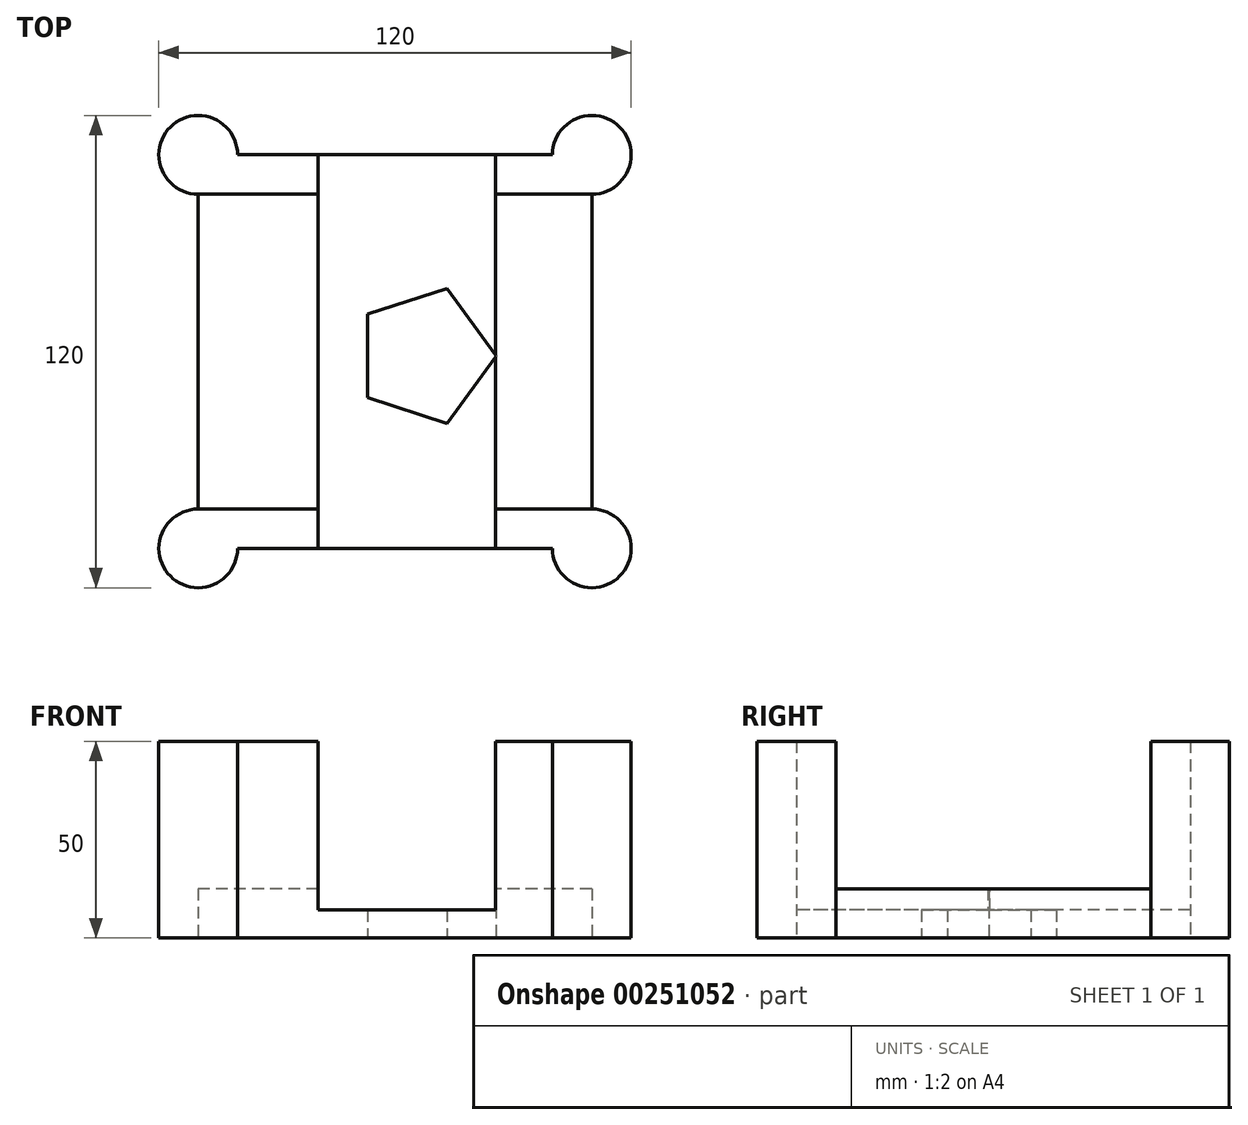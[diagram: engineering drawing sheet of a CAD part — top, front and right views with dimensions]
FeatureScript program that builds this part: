
annotation { "Feature Type Name" : "Feature", "Feature Type Description" : "" }
export const myFeature = defineFeature(function(context is Context, id is Id, definition is map)
    precondition{}
    {
        {
            var Q0;
            Q0=qCreatedBy(makeId("Top.planeOp"),FACE);
            var sketch = newSketch(context, id + "F0", { "sketchPlane" : qUnion([Q0])});
            skLineSegment(sketch, "E0.bottom", {"start": v(-57.64, -48.48) * mm, "end": v(42.36, -48.48) * mm});
            skLineSegment(sketch, "E0.top", {"start": v(-57.64, 51.52) * mm, "end": v(42.36, 51.52) * mm});
            skLineSegment(sketch, "E0.left", {"start": v(-57.64, -48.48) * mm, "end": v(-57.64, 51.52) * mm});
            skLineSegment(sketch, "E0.right", {"start": v(42.36, -48.48) * mm, "end": v(42.36, 51.52) * mm});
            skSolve(sketch);
        }
        {
            var Q0;
            Q0 = qSketchRegion(id + "F0", true);
            extrude(context, id + "F1", {"entities" : qUnion([Q0]), "depth" : 50 * mm});
        }
        {
            var Q0;
            Q0=makeQuery(id+"F1.opExtrude","SWEPT_FACE",FACE,{"disambiguationData":[OSD([sQuery(id+"F0.wireOp",EDGE,"E0.bottom")])]});
            var sketch = newSketch(context, id + "F2", { "sketchPlane" : qUnion([Q0])});
            skLineSegment(sketch, "E1.bottom", {"start": v(-27.14, 52.1) * mm, "end": v(17.86, 52.1) * mm});
            skLineSegment(sketch, "E1.top", {"start": v(-27.14, 7.1) * mm, "end": v(17.86, 7.1) * mm});
            skLineSegment(sketch, "E1.left", {"start": v(-27.14, 52.1) * mm, "end": v(-27.14, 7.1) * mm});
            skLineSegment(sketch, "E1.right", {"start": v(17.86, 52.1) * mm, "end": v(17.86, 7.1) * mm});
            skPoint(sketch, "E2.firstSnap0", {"position": v(-4.64, 52.1) * mm});
            skLineSegment(sketch, "E2.bottom", {"start": v(0, 52.1) * mm, "end": v(0, 52.1) * mm});
            skLineSegment(sketch, "E2.top", {"start": v(0, 33.97) * mm, "end": v(0, 33.97) * mm});
            skLineSegment(sketch, "E2.left", {"start": v(0, 52.1) * mm, "end": v(0, 33.97) * mm});
            skLineSegment(sketch, "E2.right", {"start": v(0, 52.1) * mm, "end": v(0, 33.97) * mm});
            skSolve(sketch);
        }
        {
            var Q0;
            Q0 = qSketchRegion(id + "F2", true);
            extrude(context, id + "F3", {"entities" : qUnion([Q0]), "operationType" : NewBodyOperationType.REMOVE, "oppositeDirection" : true, "depth" : 100 * mm});
        }
        {
            var Q0;
            Q0=makeQuery(id+"F1.opExtrude","CAP_FACE",FACE,{"disambiguationData":[OSD([sQuery(id+"F0.wireOp",EDGE,"E0.bottom"),sQuery(id+"F0.wireOp",EDGE,"E0.top"),sQuery(id+"F0.wireOp",EDGE,"E0.left"),sQuery(id+"F0.wireOp",EDGE,"E0.right")])],"isStart":true});
            var sketch = newSketch(context, id + "F4", { "sketchPlane" : qUnion([Q0])});
            skCircle(sketch, "E3", {"center": v(-57.64, -51.52) * mm, "radius": 10 * mm});
            skCircle(sketch, "E4", {"center": v(-57.64, 48.48) * mm, "radius": 10 * mm});
            skCircle(sketch, "E5", {"center": v(42.36, 48.48) * mm, "radius": 10 * mm});
            skCircle(sketch, "E6", {"center": v(42.36, -51.52) * mm, "radius": 10 * mm});
            skSolve(sketch);
        }
        {
            var Q0;
            Q0 = qSketchRegion(id + "F4", true);
            extrude(context, id + "F5", {"entities" : qUnion([Q0]), "operationType" : NewBodyOperationType.ADD, "oppositeDirection" : true, "depth" : 50 * mm});
        }
        {
            var Q0;
            Q0=makeQuery(id+"F5.boolean.opBoolean","MERGE",FACE,{"derivedFrom":[makeQuery(id+"F1.opExtrude","CAP_FACE",FACE,{"disambiguationData":[OSD([sQuery(id+"F0.wireOp",EDGE,"E0.bottom"),sQuery(id+"F0.wireOp",EDGE,"E0.top"),sQuery(id+"F0.wireOp",EDGE,"E0.left"),sQuery(id+"F0.wireOp",EDGE,"E0.right")])],"isStart":true}),makeQuery(id+"F5.opExtrude","CAP_FACE",FACE,{"disambiguationData":[OSD([sQuery(id+"F4.wireOp",EDGE,"E3")])],"isStart":true}),makeQuery(id+"F5.opExtrude","CAP_FACE",FACE,{"disambiguationData":[OSD([sQuery(id+"F4.wireOp",EDGE,"E4")])],"isStart":true}),makeQuery(id+"F5.opExtrude","CAP_FACE",FACE,{"disambiguationData":[OSD([sQuery(id+"F4.wireOp",EDGE,"E5")])],"isStart":true}),makeQuery(id+"F5.opExtrude","CAP_FACE",FACE,{"disambiguationData":[OSD([sQuery(id+"F4.wireOp",EDGE,"E6")])],"isStart":true})]});
            var sketch = newSketch(context, id + "F6", { "sketchPlane" : qUnion([Q0])});
            skCircle(sketch, "E7.cCircle", {"center": v(0, -0.43) * mm, "radius": 14.59 * mm, "construction": true});
            skLineSegment(sketch, "E7.0", {"start": v(-14.59, -11.03) * mm, "end": v(-14.59, 10.16) * mm});
            skLineSegment(sketch, "E7.1", {"start": v(-14.59, 10.16) * mm, "end": v(5.57, 16.71) * mm});
            skLineSegment(sketch, "E7.2", {"start": v(5.57, 16.71) * mm, "end": v(18.03, -0.43) * mm});
            skLineSegment(sketch, "E7.3", {"start": v(18.03, -0.43) * mm, "end": v(5.57, -17.58) * mm});
            skLineSegment(sketch, "E7.4", {"start": v(5.57, -17.58) * mm, "end": v(-14.59, -11.03) * mm});
            skPoint(sketch, "E7.0.midPoint", {"position": v(-14.59, -0.43) * mm});
            skSolve(sketch);
        }
        {
            var Q0;
            Q0 = qSketchRegion(id + "F6", true);
            extrude(context, id + "F7", {"entities" : qUnion([Q0]), "operationType" : NewBodyOperationType.REMOVE, "oppositeDirection" : true, "depth" : 25 * mm});
        }
        {
            var Q0;
            Q0=makeQuery(id+"F1.opExtrude","SWEPT_FACE",FACE,{"disambiguationData":[OSD([sQuery(id+"F0.wireOp",EDGE,"E0.left")])]});
            var sketch = newSketch(context, id + "F8", { "sketchPlane" : qUnion([Q0])});
            skLineSegment(sketch, "E8.bottom", {"start": v(38.48, 12.55) * mm, "end": v(-41.52, 12.55) * mm});
            skLineSegment(sketch, "E8.top", {"start": v(38.48, 50) * mm, "end": v(-41.52, 50) * mm});
            skLineSegment(sketch, "E8.left", {"start": v(38.48, 12.55) * mm, "end": v(38.48, 50) * mm});
            skLineSegment(sketch, "E8.right", {"start": v(-41.52, 12.55) * mm, "end": v(-41.52, 50) * mm});
            skSolve(sketch);
        }
        {
            var Q0;
            Q0 = qSketchRegion(id + "F8", true);
            extrude(context, id + "F9", {"entities" : qUnion([Q0]), "operationType" : NewBodyOperationType.REMOVE, "oppositeDirection" : true, "depth" : 150 * mm});
        }
    });
